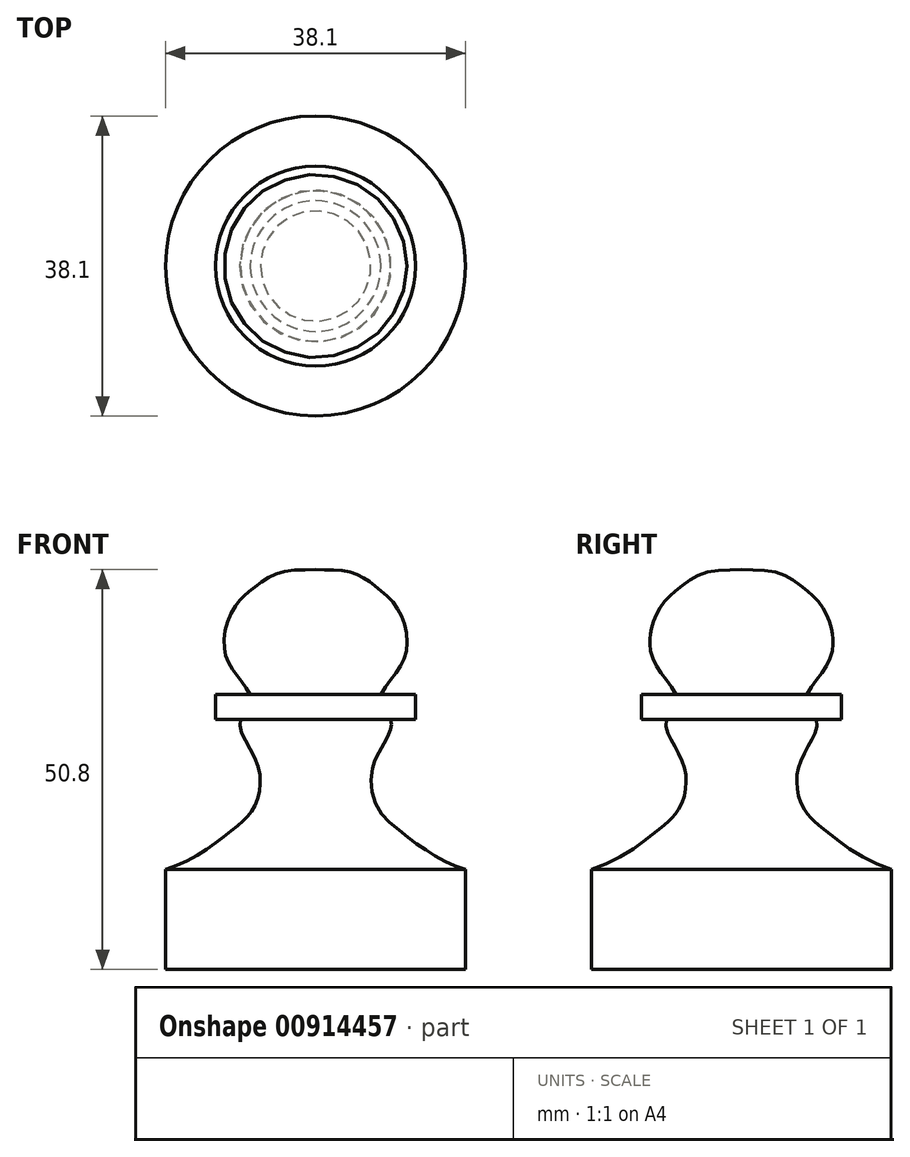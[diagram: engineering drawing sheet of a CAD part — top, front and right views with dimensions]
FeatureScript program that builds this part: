
annotation { "Feature Type Name" : "Feature", "Feature Type Description" : "" }
export const myFeature = defineFeature(function(context is Context, id is Id, definition is map)
    precondition{}
    {
        {
            var Q0;
            Q0=qCreatedBy(makeId("Front.planeOp"),FACE);
            var sketch = newSketch(context, id + "F0", { "sketchPlane" : qUnion([Q0])});
            skLineSegment(sketch, "E0", {"start": v(0, 0) * mm, "end": v(0, 50.8) * mm});
            skLineSegment(sketch, "E1", {"start": v(0, 0) * mm, "end": v(19.05, 0) * mm});
            skLineSegment(sketch, "E2", {"start": v(19.05, 0) * mm, "end": v(19.05, 12.7) * mm});
            skLineSegment(sketch, "E3", {"start": v(0, 31.75) * mm, "end": v(25, 31.75) * mm, "construction": true});
            skFitSpline(sketch, "E4", {"points": [v(19.05, 12.7) * mm, v(10.46, 17.8) * mm, v(7.73, 20.8) * mm, v(7.43, 26.21) * mm, v(9.53, 31.75) * mm], "startDerivative": vector(-32.06, 9.33) * mm, "endDerivative": vector(-7.23, 16.5) * mm});
            skLineSegment(sketch, "E5.bottom", {"start": v(0, 31.75) * mm, "end": v(12.7, 31.75) * mm});
            skLineSegment(sketch, "E5.top", {"start": v(0, 34.92) * mm, "end": v(12.7, 34.92) * mm});
            skLineSegment(sketch, "E5.left", {"start": v(0, 31.75) * mm, "end": v(0, 34.92) * mm});
            skLineSegment(sketch, "E5.right", {"start": v(12.7, 31.75) * mm, "end": v(12.7, 34.92) * mm});
            skFitSpline(sketch, "E6", {"points": [v(8.3, 34.92) * mm, v(10.25, 37.7) * mm, v(11.52, 40.35) * mm, v(11.28, 43.9) * mm, v(9.87, 46.61) * mm, v(7.73, 48.59) * mm, v(5.9, 49.86) * mm, v(3.48, 50.65) * mm, v(0, 50.8) * mm], "startDerivative": vector(11.68, 22.64) * mm, "endDerivative": vector(-26.04, 2.23) * mm});
            skSolve(sketch);
        }
        {
            var Q0;
            {var subQ7=sQuery(id+"F0.wireOp",EDGE,"E5.right");Q0=makeQuery(id+"F0.imprint","IMPRINT",FACE,{"disambiguationData":[TD([[makeQuery(id+"F0.imprint","IMPRINT",EDGE,{"derivedFrom":subQ7}),1.0]])]});}
            var Q1;
            {var subQ3=sQuery(id+"F0.wireOp",EDGE,"E6");Q1=makeQuery(id+"F0.imprint","IMPRINT",FACE,{"disambiguationData":[TD([[makeQuery(id+"F0.imprint","IMPRINT",EDGE,{"derivedFrom":subQ3}),1.0]])]});}
            var Q2;
            {var subQ0=sQuery(id+"F0.wireOp",EDGE,"E1");Q2=makeQuery(id+"F0.imprint","IMPRINT",FACE,{"disambiguationData":[TD([[makeQuery(id+"F0.imprint","IMPRINT",EDGE,{"derivedFrom":subQ0}),1.0]])]});}
            var Q3;
            Q3=sQuery(id+"F0.wireOp",EDGE,"E0");
            revolve(context, id + "F1", {"surfaceOperationType" : NewSurfaceOperationType.NEW, "entities" : qUnion([Q0, Q1, Q2]), "axis" : qUnion([Q3]), "revolveType" : RevolveType.FULL});
        }
    });
